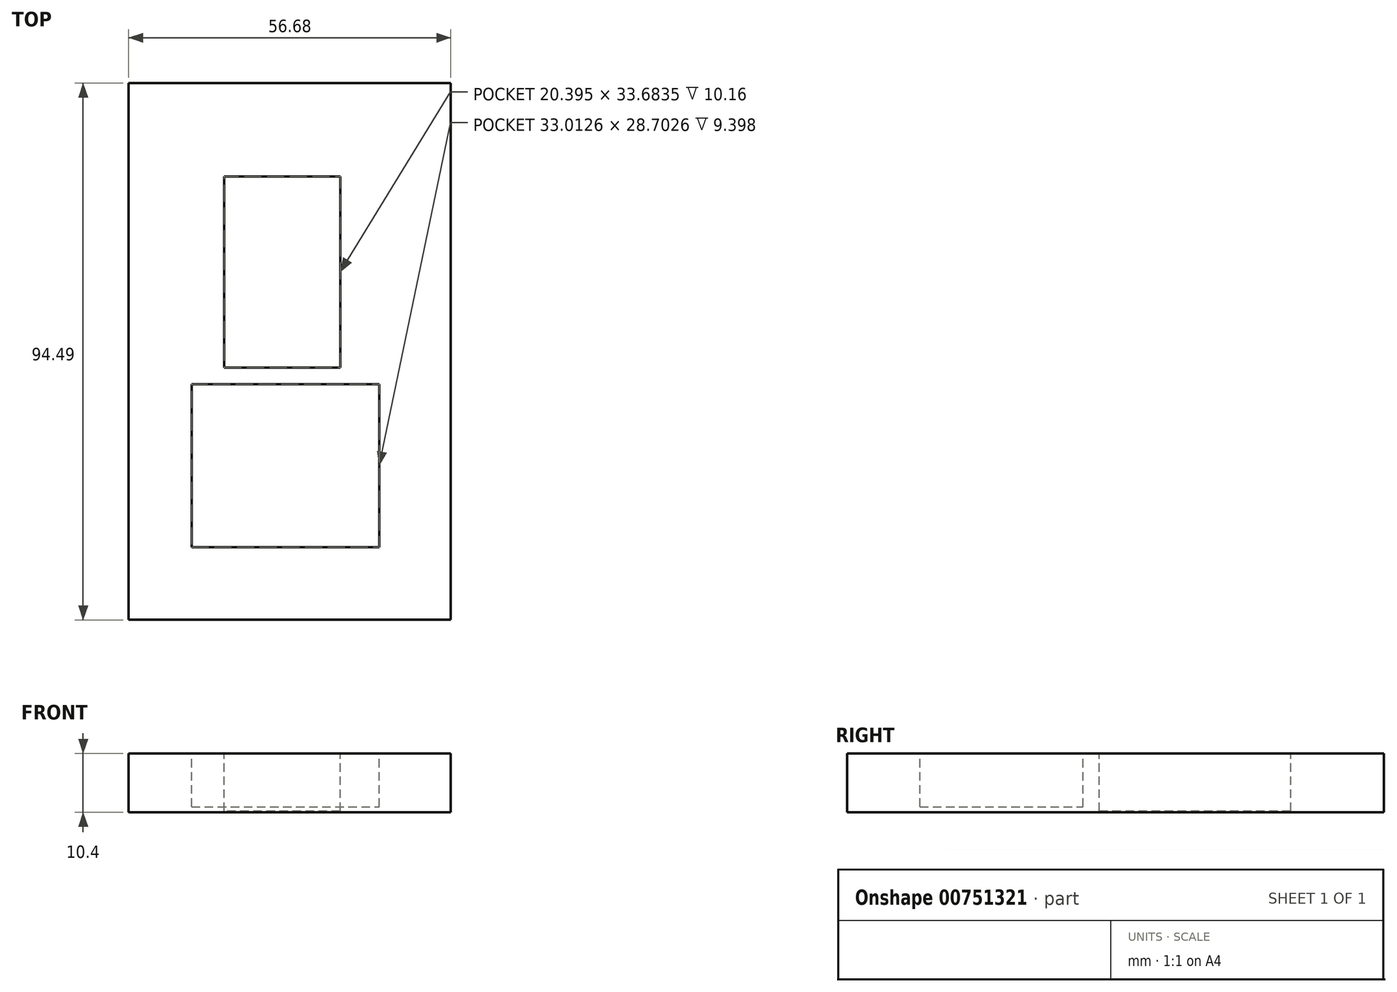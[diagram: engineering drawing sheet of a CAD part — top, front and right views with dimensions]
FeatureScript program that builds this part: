
annotation { "Feature Type Name" : "Feature", "Feature Type Description" : "" }
export const myFeature = defineFeature(function(context is Context, id is Id, definition is map)
    precondition{}
    {
        {
            var Q0;
            Q0=qCreatedBy(makeId("Front.planeOp"),FACE);
            var sketch = newSketch(context, id + "F0", { "sketchPlane" : qUnion([Q0])});
            skLineSegment(sketch, "E0", {"start": v(-36.82, 27.75) * mm, "end": v(-36.82, 17.35) * mm});
            skLineSegment(sketch, "E1", {"start": v(-36.82, 17.35) * mm, "end": v(19.86, 17.35) * mm});
            skLineSegment(sketch, "E2", {"start": v(19.86, 17.35) * mm, "end": v(19.86, 27.75) * mm});
            skLineSegment(sketch, "E3", {"start": v(-36.82, 27.75) * mm, "end": v(19.86, 27.75) * mm});
            skSolve(sketch);
        }
        {
            var Q0;
            Q0=makeQuery(id+"F0.imprint","IMPRINT",FACE,{"disambiguationData":[TD([[makeQuery(id+"F0.imprint","IMPRINT",EDGE,{"derivedFrom":sQuery(id+"F0.wireOp",EDGE,"E0")}),1.0]])]});
            extrude(context, id + "F1", {"entities" : qUnion([Q0]), "depth" : 94.49 * mm, "offsetDistance" : 25.4 * mm});
        }
        {
            var Q0;
            Q0=makeQuery(id+"F1.opExtrude","SWEPT_FACE",FACE,{"disambiguationData":[OSD([sQuery(id+"F0.wireOp",EDGE,"E3")])]});
            var sketch = newSketch(context, id + "F2", { "sketchPlane" : qUnion([Q0])});
            skLineSegment(sketch, "E4.bottom", {"start": v(-27.39, -36.47) * mm, "end": v(11.17, -36.47) * mm});
            skLineSegment(sketch, "E4.top", {"start": v(-27.39, -91.17) * mm, "end": v(11.17, -91.17) * mm});
            skLineSegment(sketch, "E4.left", {"start": v(-27.39, -36.47) * mm, "end": v(-27.39, -91.17) * mm});
            skLineSegment(sketch, "E4.right", {"start": v(11.17, -36.47) * mm, "end": v(11.17, -91.17) * mm});
            skLineSegment(sketch, "E5", {"start": v(-24.7, -1.88) * mm, "end": v(-24.7, -33.56) * mm});
            skLineSegment(sketch, "E6", {"start": v(-24.7, -33.56) * mm, "end": v(6.5, -33.56) * mm});
            skLineSegment(sketch, "E7", {"start": v(6.5, -33.56) * mm, "end": v(6.5, -1.88) * mm});
            skLineSegment(sketch, "E8", {"start": v(6.5, -1.88) * mm, "end": v(-24.7, -1.88) * mm});
            skSolve(sketch);
        }
        {
            var Q0;
            Q0=makeQuery(id+"F2.imprint","IMPRINT",FACE,{"disambiguationData":[TD([[makeQuery(id+"F2.imprint","IMPRINT",EDGE,{"derivedFrom":sQuery(id+"F2.wireOp",EDGE,"E5")}),1.0]])]});
            extrude(context, id + "F3", {"entities" : qUnion([Q0]), "operationType" : NewBodyOperationType.ADD, "depth" : -2.54 * mm, "offsetDistance" : 25.4 * mm});
        }
        {
            var Q0;
            Q0=makeQuery(id+"F1.opExtrude","SWEPT_FACE",FACE,{"disambiguationData":[OSD([sQuery(id+"F0.wireOp",EDGE,"E3")])]});
            var sketch = newSketch(context, id + "F4", { "sketchPlane" : qUnion([Q0])});
            skLineSegment(sketch, "E9.bottom", {"start": v(0.41, -16.4) * mm, "end": v(-19.98, -16.4) * mm});
            skLineSegment(sketch, "E9.top", {"start": v(0.41, -50.09) * mm, "end": v(-19.98, -50.09) * mm});
            skLineSegment(sketch, "E9.left", {"start": v(0.41, -16.4) * mm, "end": v(0.41, -50.09) * mm});
            skLineSegment(sketch, "E9.right", {"start": v(-19.98, -16.4) * mm, "end": v(-19.98, -50.09) * mm});
            skSolve(sketch);
        }
        {
            var Q0;
            Q0=makeQuery(id+"F4.imprint","IMPRINT",FACE,{"disambiguationData":[TD([[makeQuery(id+"F4.imprint","IMPRINT",EDGE,{"derivedFrom":sQuery(id+"F4.wireOp",EDGE,"E9.bottom")}),1.0]])]});
            extrude(context, id + "F5", {"entities" : qUnion([Q0]), "operationType" : NewBodyOperationType.REMOVE, "oppositeDirection" : true, "depth" : 10.16 * mm, "offsetDistance" : 25.4 * mm});
        }
        {
            var Q0;
            Q0=makeQuery(id+"F1.opExtrude","SWEPT_FACE",FACE,{"disambiguationData":[OSD([sQuery(id+"F0.wireOp",EDGE,"E3")])]});
            var sketch = newSketch(context, id + "F6", { "sketchPlane" : qUnion([Q0])});
            skLineSegment(sketch, "E10.bottom", {"start": v(-25.75, -81.7) * mm, "end": v(7.27, -81.7) * mm});
            skLineSegment(sketch, "E10.top", {"start": v(-25.75, -53) * mm, "end": v(7.27, -53) * mm});
            skLineSegment(sketch, "E10.left", {"start": v(-25.75, -81.7) * mm, "end": v(-25.75, -53) * mm});
            skLineSegment(sketch, "E10.right", {"start": v(7.27, -81.7) * mm, "end": v(7.27, -53) * mm});
            skSolve(sketch);
        }
        {
            var Q0;
            Q0=makeQuery(id+"F6.imprint","IMPRINT",FACE,{"disambiguationData":[TD([[makeQuery(id+"F6.imprint","IMPRINT",EDGE,{"derivedFrom":sQuery(id+"F6.wireOp",EDGE,"E10.bottom")}),1.0]])]});
            extrude(context, id + "F7", {"entities" : qUnion([Q0]), "operationType" : NewBodyOperationType.REMOVE, "oppositeDirection" : true, "depth" : 9.4 * mm, "offsetDistance" : 25.4 * mm});
        }
    });
